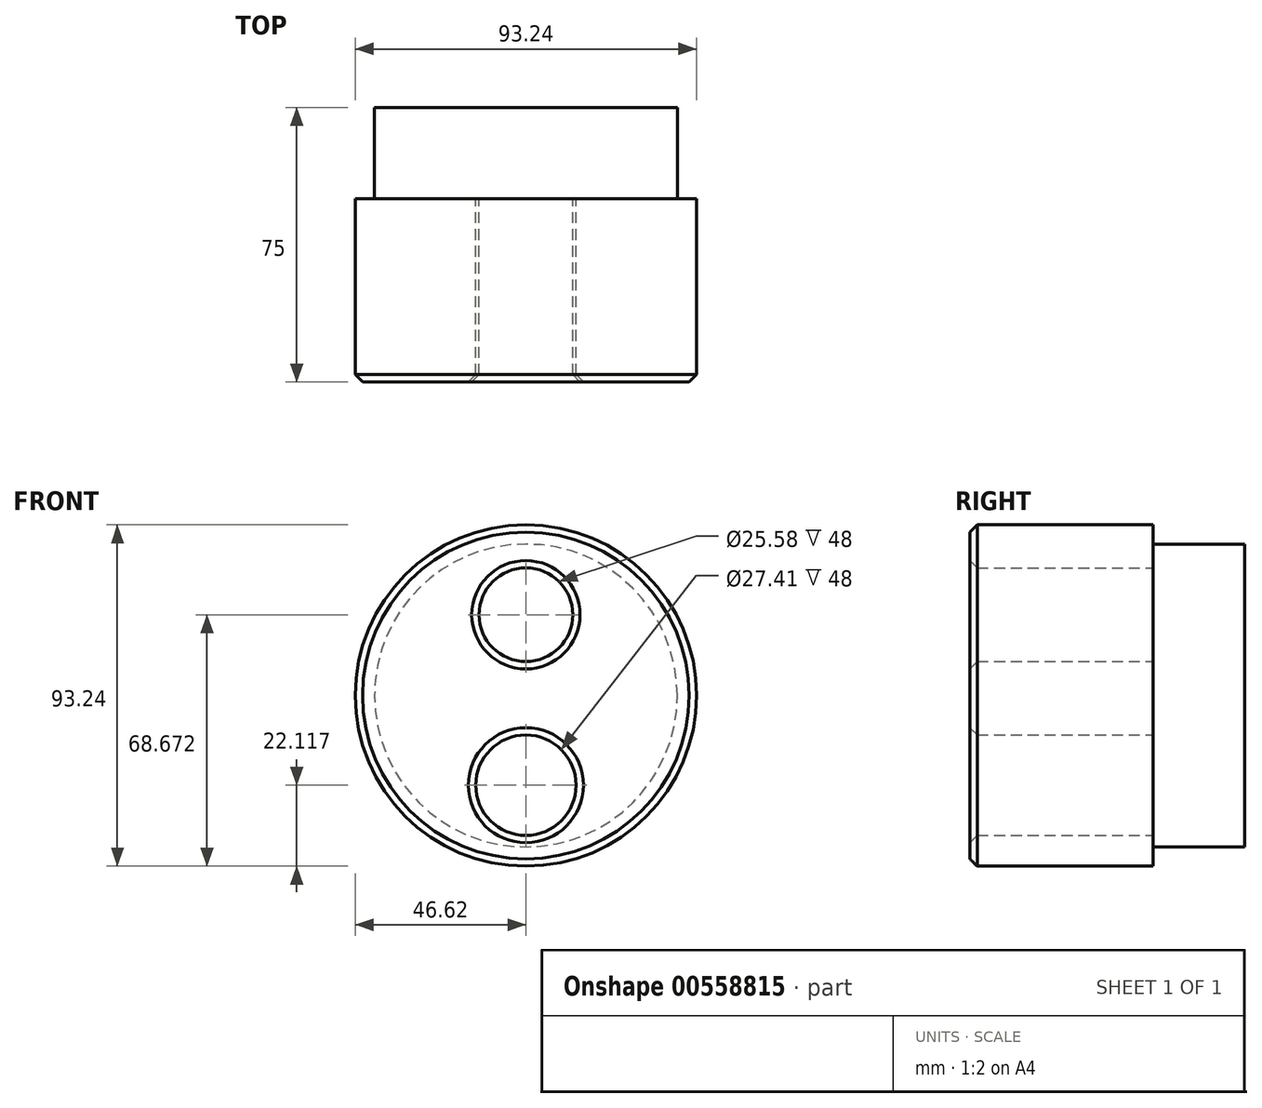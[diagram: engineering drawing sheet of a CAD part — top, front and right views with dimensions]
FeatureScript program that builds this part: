
annotation { "Feature Type Name" : "Feature", "Feature Type Description" : "" }
export const myFeature = defineFeature(function(context is Context, id is Id, definition is map)
    precondition{}
    {
        {
            var Q0;
            Q0=qCreatedBy(makeId("Front.planeOp"),FACE);
            var sketch = newSketch(context, id + "F0", { "sketchPlane" : qUnion([Q0])});
            skCircle(sketch, "E0", {"center": v(0, 0) * mm, "radius": 46.62 * mm});
            skCircle(sketch, "E1", {"center": v(0, 22.05) * mm, "radius": 12.8 * mm});
            skCircle(sketch, "E2", {"center": v(0, -24.5) * mm, "radius": 13.7 * mm});
            skSolve(sketch);
        }
        {
            var Q0;
            Q0 = qSketchRegion(id + "F0", true);
            extrude(context, id + "F1", {"entities" : qUnion([Q0]), "depth" : 50 * mm, "offsetDistance" : 25 * mm});
        }
        {
            var Q0;
            Q0=makeQuery(id+"F1.opExtrude","CAP_FACE",FACE,{"disambiguationData":[OSD([sQuery(id+"F0.wireOp",EDGE,"E0"),sQuery(id+"F0.wireOp",EDGE,"E1"),sQuery(id+"F0.wireOp",EDGE,"E2")])],"isStart":false});
            chamfer(context, id + "F2", {"entities" : qUnion([Q0]), "width" : 2 * mm, "tangentPropagation" : true});
        }
        {
            var Q0;
            Q0=qCreatedBy(makeId("Front.planeOp"),FACE);
            var sketch = newSketch(context, id + "F3", { "sketchPlane" : qUnion([Q0])});
            skCircle(sketch, "E3", {"center": v(0, 0) * mm, "radius": 41.35 * mm});
            skSolve(sketch);
        }
        {
            var Q0;
            Q0=makeQuery(id+"F3.imprint","IMPRINT",FACE,{"disambiguationData":[TD([[makeQuery(id+"F3.imprint","IMPRINT",EDGE,{"derivedFrom":sQuery(id+"F3.wireOp",EDGE,"E3")}),1.0]])]});
            var Q1;
            Q1=sQuery(id+"F3.wireOp",EDGE,"E3");
            extrude(context, id + "F4", {"entities" : qUnion([Q0]), "operationType" : NewBodyOperationType.ADD, "surfaceEntities" : qUnion([Q1]), "oppositeDirection" : true, "depth" : 25 * mm, "offsetDistance" : 25 * mm});
        }
    });
